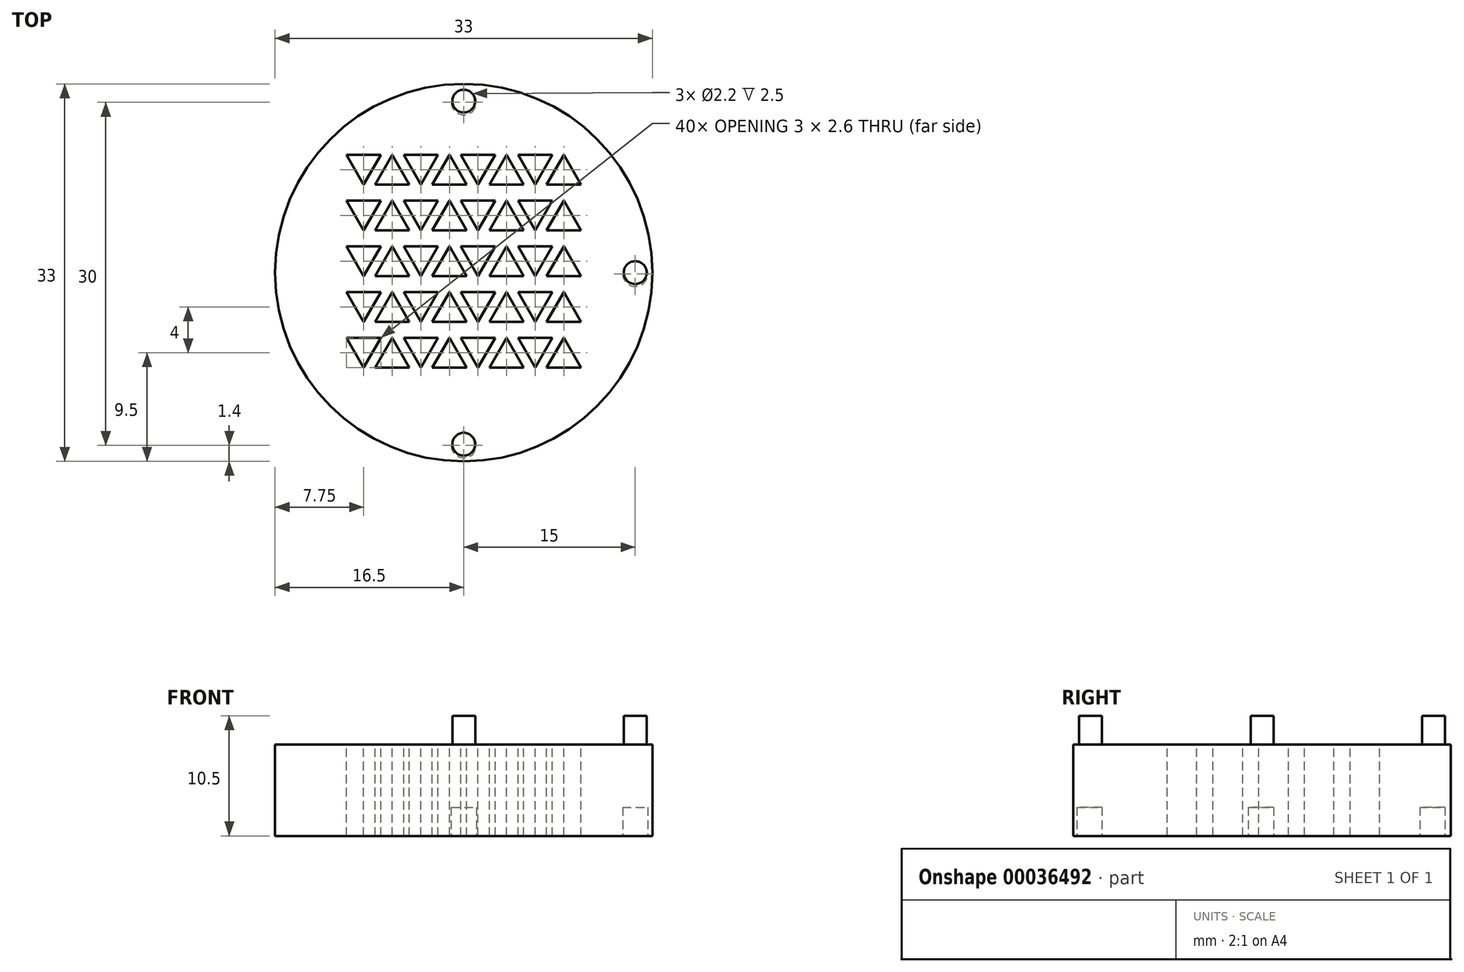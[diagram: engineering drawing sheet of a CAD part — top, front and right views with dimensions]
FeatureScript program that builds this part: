
annotation { "Feature Type Name" : "Feature", "Feature Type Description" : "" }
export const myFeature = defineFeature(function(context is Context, id is Id, definition is map)
    precondition{}
    {
        {
            var Q0;
            Q0=qCreatedBy(makeId("Top.planeOp"),FACE);
            var sketch = newSketch(context, id + "F0", { "sketchPlane" : qUnion([Q0])});
            skCircle(sketch, "E0", {"center": v(0, 0) * mm, "radius": 16.5 * mm});
            skSolve(sketch);
        }
        {
            var Q0;
            Q0=qSketchRegion(id+"F0",true);
            extrude(context, id + "F1", {"entities" : qUnion([Q0]), "depth" : 8 * mm});
        }
        {
            var Q0;
            Q0=makeQuery(id+"F1.opExtrude","CAP_FACE",FACE,{"disambiguationData":[OSD([sQuery(id+"F0.wireOp",EDGE,"E0")])],"isStart":true});
            var sketch = newSketch(context, id + "F2", { "sketchPlane" : qUnion([Q0])});
            skCircle(sketch, "E1", {"center": v(0, 15.1) * mm, "radius": 1.1 * mm});
            skCircle(sketch, "E2.1.0", {"center": v(15, 0.1) * mm, "radius": 1.1 * mm});
            skCircle(sketch, "E2.2.0", {"center": v(0, -14.9) * mm, "radius": 1.1 * mm});
            skPoint(sketch, "E2.center", {"position": v(0, 0.1) * mm});
            skLineSegment(sketch, "E2.anchor1", {"start": v(0, 0.1) * mm, "end": v(0, 15.1) * mm, "construction": true});
            skLineSegment(sketch, "E2.anchor2", {"start": v(0, 0.1) * mm, "end": v(0, -14.9) * mm, "construction": true});
            skSolve(sketch);
        }
        {
            var Q0;
            Q0=qSketchRegion(id+"F2",true);
            extrude(context, id + "F3", {"entities" : qUnion([Q0]), "operationType" : NewBodyOperationType.REMOVE, "oppositeDirection" : true, "depth" : 2.5 * mm});
        }
        {
            var Q0;
            Q0=makeQuery(id+"F1.opExtrude","CAP_FACE",FACE,{"disambiguationData":[OSD([sQuery(id+"F0.wireOp",EDGE,"E0")])],"isStart":false});
            var sketch = newSketch(context, id + "F4", { "sketchPlane" : qUnion([Q0])});
            skCircle(sketch, "E3", {"center": v(0, 15) * mm, "radius": 1 * mm});
            skCircle(sketch, "E4.1.0", {"center": v(15, 0) * mm, "radius": 1 * mm});
            skCircle(sketch, "E4.2.0", {"center": v(0, -15) * mm, "radius": 1 * mm});
            skPoint(sketch, "E4.center", {"position": v(0, 0) * mm});
            skLineSegment(sketch, "E4.anchor1", {"start": v(0, 0) * mm, "end": v(0, 15) * mm, "construction": true});
            skLineSegment(sketch, "E4.anchor2", {"start": v(0, 0) * mm, "end": v(0, -15) * mm, "construction": true});
            skSolve(sketch);
        }
        {
            var Q0;
            Q0=qSketchRegion(id+"F4",true);
            extrude(context, id + "F5", {"entities" : qUnion([Q0]), "operationType" : NewBodyOperationType.ADD, "depth" : 2.5 * mm});
        }
        {
            var Q0;
            Q0=makeQuery(id+"F1.opExtrude","CAP_FACE",FACE,{"disambiguationData":[OSD([sQuery(id+"F0.wireOp",EDGE,"E0")])],"isStart":false});
            var sketch = newSketch(context, id + "F6", { "sketchPlane" : qUnion([Q0])});
            skCircle(sketch, "E5.cCircle", {"center": v(-8.75, -6.57) * mm, "radius": 0.87 * mm, "construction": true});
            skLineSegment(sketch, "E5.0", {"start": v(-10.25, -5.7) * mm, "end": v(-7.25, -5.7) * mm});
            skLineSegment(sketch, "E5.1", {"start": v(-7.25, -5.7) * mm, "end": v(-8.75, -8.3) * mm});
            skLineSegment(sketch, "E5.2", {"start": v(-8.75, -8.3) * mm, "end": v(-10.25, -5.7) * mm});
            skPoint(sketch, "E5.0.midPoint", {"position": v(-8.75, -5.7) * mm});
            skPoint(sketch, "E6.0.midPoint", {"position": v(-4.16, -8.82) * mm});
            skLineSegment(sketch, "E7", {"start": v(-7.75, -8.3) * mm, "end": v(-4.75, -8.3) * mm});
            skLineSegment(sketch, "E8", {"start": v(-7.75, -8.3) * mm, "end": v(-6.25, -5.7) * mm});
            skLineSegment(sketch, "E9", {"start": v(-6.25, -5.7) * mm, "end": v(-4.75, -8.3) * mm});
            skLineSegment(sketch, "E10.0.1.0", {"start": v(-10.25, -1.7) * mm, "end": v(-7.25, -1.7) * mm});
            skLineSegment(sketch, "E10.0.1.1", {"start": v(-8.75, -4.3) * mm, "end": v(-10.25, -1.7) * mm});
            skLineSegment(sketch, "E10.0.1.2", {"start": v(-7.25, -1.7) * mm, "end": v(-8.75, -4.3) * mm});
            skLineSegment(sketch, "E10.0.1.3", {"start": v(-7.75, -4.3) * mm, "end": v(-6.25, -1.7) * mm});
            skLineSegment(sketch, "E10.0.1.4", {"start": v(-7.75, -4.3) * mm, "end": v(-4.75, -4.3) * mm});
            skLineSegment(sketch, "E10.0.1.5", {"start": v(-6.25, -1.7) * mm, "end": v(-4.75, -4.3) * mm});
            skLineSegment(sketch, "E10.0.2.0", {"start": v(-10.25, 2.3) * mm, "end": v(-7.25, 2.3) * mm});
            skLineSegment(sketch, "E10.0.2.1", {"start": v(-8.75, -0.3) * mm, "end": v(-10.25, 2.3) * mm});
            skLineSegment(sketch, "E10.0.2.2", {"start": v(-7.25, 2.3) * mm, "end": v(-8.75, -0.3) * mm});
            skLineSegment(sketch, "E10.0.2.3", {"start": v(-7.75, -0.3) * mm, "end": v(-6.25, 2.3) * mm});
            skLineSegment(sketch, "E10.0.2.4", {"start": v(-7.75, -0.3) * mm, "end": v(-4.75, -0.3) * mm});
            skLineSegment(sketch, "E10.0.2.5", {"start": v(-6.25, 2.3) * mm, "end": v(-4.75, -0.3) * mm});
            skLineSegment(sketch, "E10.0.3.0", {"start": v(-10.25, 6.3) * mm, "end": v(-7.25, 6.3) * mm});
            skLineSegment(sketch, "E10.0.3.1", {"start": v(-8.75, 3.7) * mm, "end": v(-10.25, 6.3) * mm});
            skLineSegment(sketch, "E10.0.3.2", {"start": v(-7.25, 6.3) * mm, "end": v(-8.75, 3.7) * mm});
            skLineSegment(sketch, "E10.0.3.3", {"start": v(-7.75, 3.7) * mm, "end": v(-6.25, 6.3) * mm});
            skLineSegment(sketch, "E10.0.3.4", {"start": v(-7.75, 3.7) * mm, "end": v(-4.75, 3.7) * mm});
            skLineSegment(sketch, "E10.0.3.5", {"start": v(-6.25, 6.3) * mm, "end": v(-4.75, 3.7) * mm});
            skLineSegment(sketch, "E10.0.4.0", {"start": v(-10.25, 10.3) * mm, "end": v(-7.25, 10.3) * mm});
            skLineSegment(sketch, "E10.0.4.1", {"start": v(-8.75, 7.7) * mm, "end": v(-10.25, 10.3) * mm});
            skLineSegment(sketch, "E10.0.4.2", {"start": v(-7.25, 10.3) * mm, "end": v(-8.75, 7.7) * mm});
            skLineSegment(sketch, "E10.0.4.3", {"start": v(-7.75, 7.7) * mm, "end": v(-6.25, 10.3) * mm});
            skLineSegment(sketch, "E10.0.4.4", {"start": v(-7.75, 7.7) * mm, "end": v(-4.75, 7.7) * mm});
            skLineSegment(sketch, "E10.0.4.5", {"start": v(-6.25, 10.3) * mm, "end": v(-4.75, 7.7) * mm});
            skLineSegment(sketch, "E10.1.0.0", {"start": v(-5.25, -5.7) * mm, "end": v(-2.25, -5.7) * mm});
            skLineSegment(sketch, "E10.1.0.1", {"start": v(-3.75, -8.3) * mm, "end": v(-5.25, -5.7) * mm});
            skLineSegment(sketch, "E10.1.0.2", {"start": v(-2.25, -5.7) * mm, "end": v(-3.75, -8.3) * mm});
            skLineSegment(sketch, "E10.1.0.3", {"start": v(-2.75, -8.3) * mm, "end": v(-1.25, -5.7) * mm});
            skLineSegment(sketch, "E10.1.0.4", {"start": v(-2.75, -8.3) * mm, "end": v(0.25, -8.3) * mm});
            skLineSegment(sketch, "E10.1.0.5", {"start": v(-1.25, -5.7) * mm, "end": v(0.25, -8.3) * mm});
            skLineSegment(sketch, "E10.1.1.0", {"start": v(-5.25, -1.7) * mm, "end": v(-2.25, -1.7) * mm});
            skLineSegment(sketch, "E10.1.1.1", {"start": v(-3.75, -4.3) * mm, "end": v(-5.25, -1.7) * mm});
            skLineSegment(sketch, "E10.1.1.2", {"start": v(-2.25, -1.7) * mm, "end": v(-3.75, -4.3) * mm});
            skLineSegment(sketch, "E10.1.1.3", {"start": v(-2.75, -4.3) * mm, "end": v(-1.25, -1.7) * mm});
            skLineSegment(sketch, "E10.1.1.4", {"start": v(-2.75, -4.3) * mm, "end": v(0.25, -4.3) * mm});
            skLineSegment(sketch, "E10.1.1.5", {"start": v(-1.25, -1.7) * mm, "end": v(0.25, -4.3) * mm});
            skLineSegment(sketch, "E10.1.2.0", {"start": v(-5.25, 2.3) * mm, "end": v(-2.25, 2.3) * mm});
            skLineSegment(sketch, "E10.1.2.1", {"start": v(-3.75, -0.3) * mm, "end": v(-5.25, 2.3) * mm});
            skLineSegment(sketch, "E10.1.2.2", {"start": v(-2.25, 2.3) * mm, "end": v(-3.75, -0.3) * mm});
            skLineSegment(sketch, "E10.1.2.3", {"start": v(-2.75, -0.3) * mm, "end": v(-1.25, 2.3) * mm});
            skLineSegment(sketch, "E10.1.2.4", {"start": v(-2.75, -0.3) * mm, "end": v(0.25, -0.3) * mm});
            skLineSegment(sketch, "E10.1.2.5", {"start": v(-1.25, 2.3) * mm, "end": v(0.25, -0.3) * mm});
            skLineSegment(sketch, "E10.1.3.0", {"start": v(-5.25, 6.3) * mm, "end": v(-2.25, 6.3) * mm});
            skLineSegment(sketch, "E10.1.3.1", {"start": v(-3.75, 3.7) * mm, "end": v(-5.25, 6.3) * mm});
            skLineSegment(sketch, "E10.1.3.2", {"start": v(-2.25, 6.3) * mm, "end": v(-3.75, 3.7) * mm});
            skLineSegment(sketch, "E10.1.3.3", {"start": v(-2.75, 3.7) * mm, "end": v(-1.25, 6.3) * mm});
            skLineSegment(sketch, "E10.1.3.4", {"start": v(-2.75, 3.7) * mm, "end": v(0.25, 3.7) * mm});
            skLineSegment(sketch, "E10.1.3.5", {"start": v(-1.25, 6.3) * mm, "end": v(0.25, 3.7) * mm});
            skLineSegment(sketch, "E10.1.4.0", {"start": v(-5.25, 10.3) * mm, "end": v(-2.25, 10.3) * mm});
            skLineSegment(sketch, "E10.1.4.1", {"start": v(-3.75, 7.7) * mm, "end": v(-5.25, 10.3) * mm});
            skLineSegment(sketch, "E10.1.4.2", {"start": v(-2.25, 10.3) * mm, "end": v(-3.75, 7.7) * mm});
            skLineSegment(sketch, "E10.1.4.3", {"start": v(-2.75, 7.7) * mm, "end": v(-1.25, 10.3) * mm});
            skLineSegment(sketch, "E10.1.4.4", {"start": v(-2.75, 7.7) * mm, "end": v(0.25, 7.7) * mm});
            skLineSegment(sketch, "E10.1.4.5", {"start": v(-1.25, 10.3) * mm, "end": v(0.25, 7.7) * mm});
            skLineSegment(sketch, "E10.2.0.0", {"start": v(-0.25, -5.7) * mm, "end": v(2.75, -5.7) * mm});
            skLineSegment(sketch, "E10.2.0.1", {"start": v(1.25, -8.3) * mm, "end": v(-0.25, -5.7) * mm});
            skLineSegment(sketch, "E10.2.0.2", {"start": v(2.75, -5.7) * mm, "end": v(1.25, -8.3) * mm});
            skLineSegment(sketch, "E10.2.0.3", {"start": v(2.25, -8.3) * mm, "end": v(3.75, -5.7) * mm});
            skLineSegment(sketch, "E10.2.0.4", {"start": v(2.25, -8.3) * mm, "end": v(5.25, -8.3) * mm});
            skLineSegment(sketch, "E10.2.0.5", {"start": v(3.75, -5.7) * mm, "end": v(5.25, -8.3) * mm});
            skLineSegment(sketch, "E10.2.1.0", {"start": v(-0.25, -1.7) * mm, "end": v(2.75, -1.7) * mm});
            skLineSegment(sketch, "E10.2.1.1", {"start": v(1.25, -4.3) * mm, "end": v(-0.25, -1.7) * mm});
            skLineSegment(sketch, "E10.2.1.2", {"start": v(2.75, -1.7) * mm, "end": v(1.25, -4.3) * mm});
            skLineSegment(sketch, "E10.2.1.3", {"start": v(2.25, -4.3) * mm, "end": v(3.75, -1.7) * mm});
            skLineSegment(sketch, "E10.2.1.4", {"start": v(2.25, -4.3) * mm, "end": v(5.25, -4.3) * mm});
            skLineSegment(sketch, "E10.2.1.5", {"start": v(3.75, -1.7) * mm, "end": v(5.25, -4.3) * mm});
            skLineSegment(sketch, "E10.2.2.0", {"start": v(-0.25, 2.3) * mm, "end": v(2.75, 2.3) * mm});
            skLineSegment(sketch, "E10.2.2.1", {"start": v(1.25, -0.3) * mm, "end": v(-0.25, 2.3) * mm});
            skLineSegment(sketch, "E10.2.2.2", {"start": v(2.75, 2.3) * mm, "end": v(1.25, -0.3) * mm});
            skLineSegment(sketch, "E10.2.2.3", {"start": v(2.25, -0.3) * mm, "end": v(3.75, 2.3) * mm});
            skLineSegment(sketch, "E10.2.2.4", {"start": v(2.25, -0.3) * mm, "end": v(5.25, -0.3) * mm});
            skLineSegment(sketch, "E10.2.2.5", {"start": v(3.75, 2.3) * mm, "end": v(5.25, -0.3) * mm});
            skLineSegment(sketch, "E10.2.3.0", {"start": v(-0.25, 6.3) * mm, "end": v(2.75, 6.3) * mm});
            skLineSegment(sketch, "E10.2.3.1", {"start": v(1.25, 3.7) * mm, "end": v(-0.25, 6.3) * mm});
            skLineSegment(sketch, "E10.2.3.2", {"start": v(2.75, 6.3) * mm, "end": v(1.25, 3.7) * mm});
            skLineSegment(sketch, "E10.2.3.3", {"start": v(2.25, 3.7) * mm, "end": v(3.75, 6.3) * mm});
            skLineSegment(sketch, "E10.2.3.4", {"start": v(2.25, 3.7) * mm, "end": v(5.25, 3.7) * mm});
            skLineSegment(sketch, "E10.2.3.5", {"start": v(3.75, 6.3) * mm, "end": v(5.25, 3.7) * mm});
            skLineSegment(sketch, "E10.2.4.0", {"start": v(-0.25, 10.3) * mm, "end": v(2.75, 10.3) * mm});
            skLineSegment(sketch, "E10.2.4.1", {"start": v(1.25, 7.7) * mm, "end": v(-0.25, 10.3) * mm});
            skLineSegment(sketch, "E10.2.4.2", {"start": v(2.75, 10.3) * mm, "end": v(1.25, 7.7) * mm});
            skLineSegment(sketch, "E10.2.4.3", {"start": v(2.25, 7.7) * mm, "end": v(3.75, 10.3) * mm});
            skLineSegment(sketch, "E10.2.4.4", {"start": v(2.25, 7.7) * mm, "end": v(5.25, 7.7) * mm});
            skLineSegment(sketch, "E10.2.4.5", {"start": v(3.75, 10.3) * mm, "end": v(5.25, 7.7) * mm});
            skLineSegment(sketch, "E10.3.0.0", {"start": v(4.75, -5.7) * mm, "end": v(7.75, -5.7) * mm});
            skLineSegment(sketch, "E10.3.0.1", {"start": v(6.25, -8.3) * mm, "end": v(4.75, -5.7) * mm});
            skLineSegment(sketch, "E10.3.0.2", {"start": v(7.75, -5.7) * mm, "end": v(6.25, -8.3) * mm});
            skLineSegment(sketch, "E10.3.0.3", {"start": v(7.25, -8.3) * mm, "end": v(8.75, -5.7) * mm});
            skLineSegment(sketch, "E10.3.0.4", {"start": v(7.25, -8.3) * mm, "end": v(10.25, -8.3) * mm});
            skLineSegment(sketch, "E10.3.0.5", {"start": v(8.75, -5.7) * mm, "end": v(10.25, -8.3) * mm});
            skLineSegment(sketch, "E10.3.1.0", {"start": v(4.75, -1.7) * mm, "end": v(7.75, -1.7) * mm});
            skLineSegment(sketch, "E10.3.1.1", {"start": v(6.25, -4.3) * mm, "end": v(4.75, -1.7) * mm});
            skLineSegment(sketch, "E10.3.1.2", {"start": v(7.75, -1.7) * mm, "end": v(6.25, -4.3) * mm});
            skLineSegment(sketch, "E10.3.1.3", {"start": v(7.25, -4.3) * mm, "end": v(8.75, -1.7) * mm});
            skLineSegment(sketch, "E10.3.1.4", {"start": v(7.25, -4.3) * mm, "end": v(10.25, -4.3) * mm});
            skLineSegment(sketch, "E10.3.1.5", {"start": v(8.75, -1.7) * mm, "end": v(10.25, -4.3) * mm});
            skLineSegment(sketch, "E10.3.2.0", {"start": v(4.75, 2.3) * mm, "end": v(7.75, 2.3) * mm});
            skLineSegment(sketch, "E10.3.2.1", {"start": v(6.25, -0.3) * mm, "end": v(4.75, 2.3) * mm});
            skLineSegment(sketch, "E10.3.2.2", {"start": v(7.75, 2.3) * mm, "end": v(6.25, -0.3) * mm});
            skLineSegment(sketch, "E10.3.2.3", {"start": v(7.25, -0.3) * mm, "end": v(8.75, 2.3) * mm});
            skLineSegment(sketch, "E10.3.2.4", {"start": v(7.25, -0.3) * mm, "end": v(10.25, -0.3) * mm});
            skLineSegment(sketch, "E10.3.2.5", {"start": v(8.75, 2.3) * mm, "end": v(10.25, -0.3) * mm});
            skLineSegment(sketch, "E10.3.3.0", {"start": v(4.75, 6.3) * mm, "end": v(7.75, 6.3) * mm});
            skLineSegment(sketch, "E10.3.3.1", {"start": v(6.25, 3.7) * mm, "end": v(4.75, 6.3) * mm});
            skLineSegment(sketch, "E10.3.3.2", {"start": v(7.75, 6.3) * mm, "end": v(6.25, 3.7) * mm});
            skLineSegment(sketch, "E10.3.3.3", {"start": v(7.25, 3.7) * mm, "end": v(8.75, 6.3) * mm});
            skLineSegment(sketch, "E10.3.3.4", {"start": v(7.25, 3.7) * mm, "end": v(10.25, 3.7) * mm});
            skLineSegment(sketch, "E10.3.3.5", {"start": v(8.75, 6.3) * mm, "end": v(10.25, 3.7) * mm});
            skLineSegment(sketch, "E10.3.4.0", {"start": v(4.75, 10.3) * mm, "end": v(7.75, 10.3) * mm});
            skLineSegment(sketch, "E10.3.4.1", {"start": v(6.25, 7.7) * mm, "end": v(4.75, 10.3) * mm});
            skLineSegment(sketch, "E10.3.4.2", {"start": v(7.75, 10.3) * mm, "end": v(6.25, 7.7) * mm});
            skLineSegment(sketch, "E10.3.4.3", {"start": v(7.25, 7.7) * mm, "end": v(8.75, 10.3) * mm});
            skLineSegment(sketch, "E10.3.4.4", {"start": v(7.25, 7.7) * mm, "end": v(10.25, 7.7) * mm});
            skLineSegment(sketch, "E10.3.4.5", {"start": v(8.75, 10.3) * mm, "end": v(10.25, 7.7) * mm});
            skLineSegment(sketch, "E10.direction1", {"start": v(-10.25, -5.7) * mm, "end": v(-5.25, -5.7) * mm, "construction": true});
            skLineSegment(sketch, "E10.direction2", {"start": v(-10.25, -5.7) * mm, "end": v(-10.25, -1.7) * mm, "construction": true});
            skLineSegment(sketch, "E11", {"start": v(-2.75, 7.7) * mm, "end": v(2.75, 10.3) * mm, "construction": true});
            skLineSegment(sketch, "E12", {"start": v(1.25, 7.7) * mm, "end": v(-1.25, 10.3) * mm, "construction": true});
            skPoint(sketch, "E13", {"position": v(0, 9) * mm});
            skLineSegment(sketch, "E14", {"start": v(0, 0) * mm, "end": v(0, 11.83) * mm, "construction": true});
            skSolve(sketch);
        }
        {
            var Q0;
            Q0 = qSketchRegion(id + "F6", true);
            extrude(context, id + "F7", {"entities" : qUnion([Q0]), "operationType" : NewBodyOperationType.REMOVE, "oppositeDirection" : true, "depth" : 25 * mm});
        }
    });
